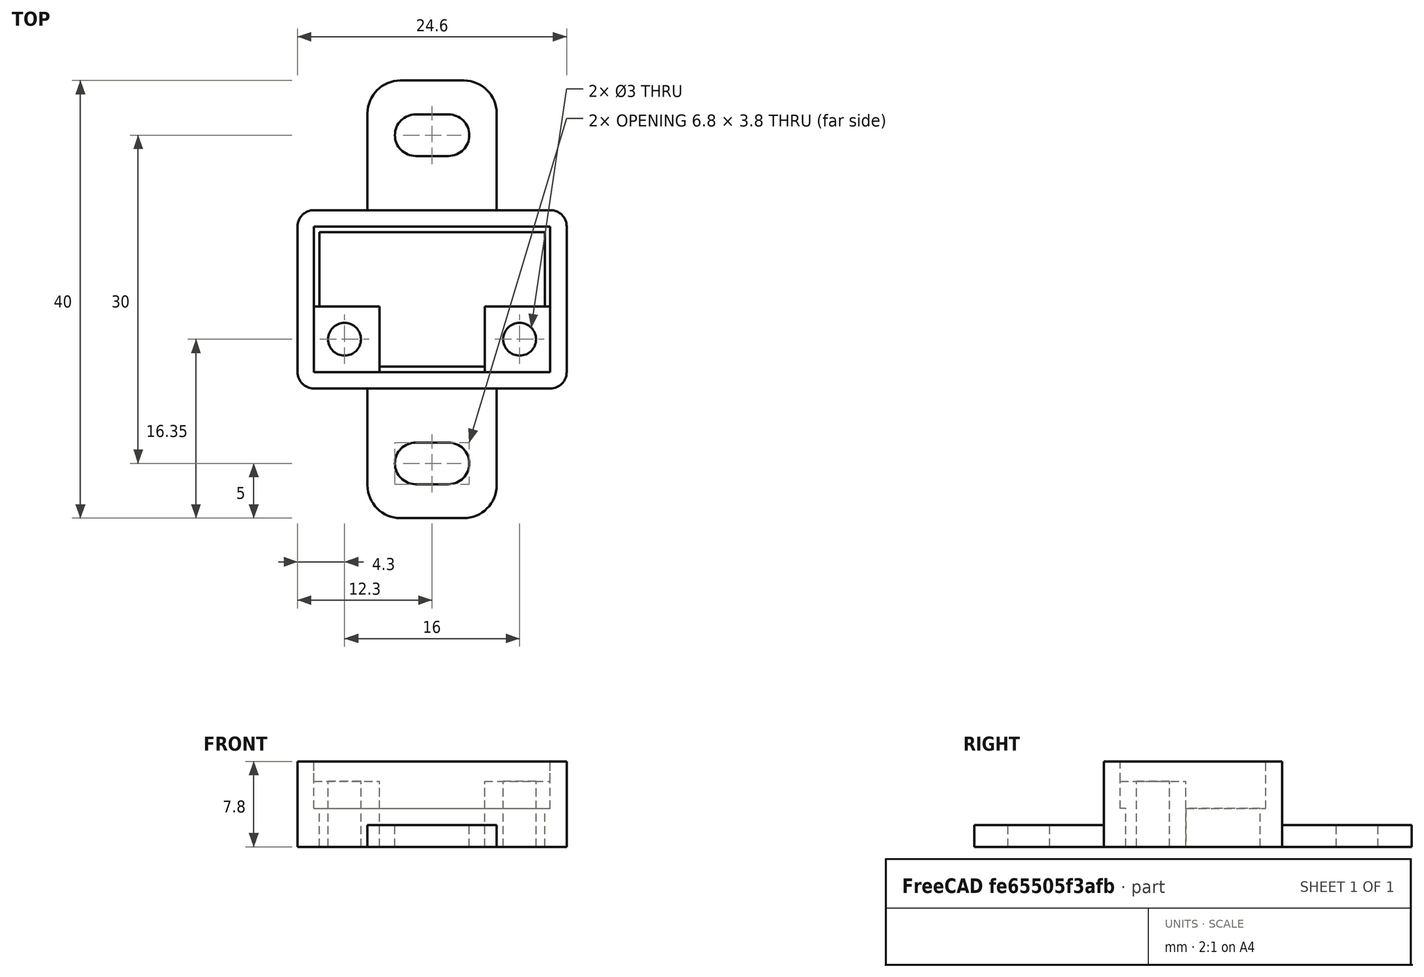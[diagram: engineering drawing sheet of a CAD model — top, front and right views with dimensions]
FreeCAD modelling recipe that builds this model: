
FCSTD DOCUMENT  (FreeCAD 0.19R)
Label: T.E._9808E
License: All rights reserved
LicenseURL: http://en.wikipedia.org/wiki/All_rights_reserved
objects: Part::Box×4, Part::MultiFuse×3, Part::FeaturePython×2, Part::Cut×2, Spreadsheet::Sheet×1, Part::Cylinder×1, Part::Fillet×1, Part::Feature×1, App::Part×1
note: 14 computed .brp shape members not serialized (recipe doc carries the construction recipe); baked Part::Feature solids carry a one-line shape summary decoded from their .brp

FEATURE [Spreadsheet::Sheet] Spreadsheet  label="p"
  cells = A1=hole_x_dist; B1(hole_x_dist)=16; A2=hole_y_off; B2(hole_y_off)=3; A3=pcb_under; B3(pcb_under)=3; A4=pcb_x; B4(pcb_x)=21.6; A5=pcb_y; B5(pcb_y)=13.3; A6=hole_stand_x; B6(hole_stand_x)=6; A7=hole_stand_y; B7(hole_stand_y)=6; A8=hole_r; B8(hole_r)=1.5; A9=box_wall; B9(box_wall)=1.5; A10=under_layer; B10(under_layer)=3; A11=pcb_height; B11(pcb_height)=1.8; A12=under_pcb_border; B12(under_pcb_border)=0.5
FEATURE [Part::Box] Box  label="bottom cube"
  AttacherType = Attacher::AttachEngine3D
  Height = 7.8
  Length = 24.6
  Width = 16.3
  expr: Height = <<p>>.pcb_under + <<p>>.pcb_height + <<p>>.under_layer
  expr: Length = <<p>>.pcb_x + <<p>>.box_wall * 2
  expr: Width = <<p>>.pcb_y + <<p>>.box_wall * 2
FEATURE [Part::Box] Box001  label="bottom extraction"
  AttacherType = Attacher::AttachEngine3D
  Height = 10
  Length = 20.6
  Placement = pos=(2,2,0) rot=(0,0,1;0rad)
  Width = 12.3
  expr: Width = <<p>>.pcb_y - <<p>>.under_pcb_border * 2
  expr: Length = <<p>>.pcb_x - <<p>>.under_pcb_border * 2
  expr: .Placement.Base.x = <<p>>.under_pcb_border + <<p>>.box_wall
  expr: .Placement.Base.y = <<p>>.under_pcb_border + <<p>>.box_wall
FEATURE [Part::Box] Box002  label="pcb extraction"
  AttacherType = Attacher::AttachEngine3D
  Height = 10
  Length = 21.6
  Placement = pos=(1.5,1.5,3.5) rot=(0,0,1;0rad)
  Width = 13.3
  expr: Width = <<p>>.pcb_y
  expr: Length = <<p>>.pcb_x
  expr: .Placement.Base.x = <<p>>.box_wall
  expr: .Placement.Base.y = <<p>>.box_wall
  expr: .Placement.Base.z = <<p>>.under_pcb_border + <<p>>.under_layer
FEATURE [Part::MultiFuse] Fusion  label="bottom extraction001"
  Shapes = -> [Box001,Box002]
FEATURE [Part::Box] Box003  label="hole stand cube"
  AttacherType = Attacher::AttachEngine3D
  Height = 6
  Length = 6
  Placement = pos=(1.5,1.5,0) rot=(0,0,1;0rad)
  Width = 6
  expr: Length = <<p>>.hole_stand_x
  expr: Width = <<p>>.hole_stand_y
  expr: Height = <<p>>.pcb_under + <<p>>.under_layer
  expr: .Placement.Base.x = <<p>>.box_wall
  expr: .Placement.Base.y = <<p>>.box_wall
FEATURE [Part::FeaturePython] Array  label="hole stand array"  # Draft array (typed FeaturePython)
  Angle = 360
  ArrayType = 0
  Axis = (0,0,1)
  Base = -> Box003
  Center = (0,0,0)
  Fuse = false
  IntervalAxis = (0,0,0)
  IntervalX = (15.6,0,0)
  IntervalY = (0,7.3,0)
  IntervalZ = (0,0,1)
  NumberPolar = 1
  NumberX = 2
  NumberY = 1
  NumberZ = 1
  expr: .IntervalX.x = <<p>>.pcb_x - <<p>>.hole_stand_x
  expr: .IntervalY.y = <<p>>.pcb_y - <<p>>.hole_stand_y
FEATURE [Part::Cylinder] Cylinder  label="pcb hole"
  Angle = 360
  AttacherType = Attacher::AttachEngine3D
  Height = 10
  Placement = pos=(4.3,4.5,0) rot=(0,0,1;0rad)
  Radius = 1.5
  expr: Radius = <<p>>.hole_r
  expr: .Placement.Base.x = (<<p>>.box_wall * 2 + <<p>>.pcb_x - <<p>>.hole_x_dist) / 2
FEATURE [Part::FeaturePython] Array001  label="hole array"  # Draft array (typed FeaturePython)
  Angle = 360
  ArrayType = 0
  Axis = (0,0,1)
  Base = -> Cylinder
  Center = (0,0,0)
  Fuse = false
  IntervalAxis = (0,0,0)
  IntervalX = (16,0,0)
  IntervalY = (0,3,0)
  IntervalZ = (0,0,1)
  NumberPolar = 1
  NumberX = 2
  NumberY = 1
  NumberZ = 1
  expr: .IntervalX.x = <<p>>.hole_x_dist
  expr: .IntervalY.y = Spreadsheet.hole_y_off
FEATURE [Part::Fillet] Fillet001  label="bottom cube fillet"
  Base = -> Box
  Edges = 4 edges r=1.5: [Edge1,Edge3,Edge5,Edge7]
FEATURE [Part::Feature] Cut002002  label="attach plane y dir002"
  Placement = pos=(6.4,-11.85,0) rot=(0,0,1;0rad)
  shape: bbox 11.8 x 40 x 2 mm, 20 faces (baked)
FEATURE [Part::MultiFuse] Fusion002  label="bottom fusion"
  Shapes = -> [Fillet001,Cut002002]
FEATURE [Part::Cut] Cut  label="pcb box cut"
  Base = -> Fusion002
  Tool = -> Fusion
FEATURE [Part::MultiFuse] Fusion001  label="frame fusion"
  Shapes = -> [Array,Cut]
FEATURE [Part::Cut] Cut001  label="frame fusion with holes"
  Base = -> Fusion001
  Tool = -> Array001
FEATURE [App::Part] Part  label="body part"
  Group = -> [Fusion,Fusion002,Box002,Box003,Box001,Array001,Cut,Array,Cylinder,Fusion001,Cut001]
  Origin = -> Origin
